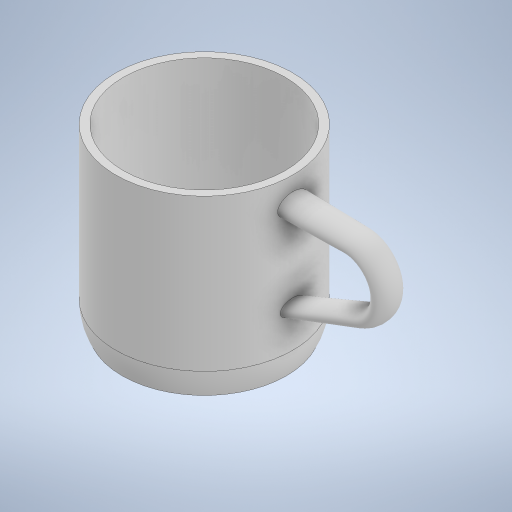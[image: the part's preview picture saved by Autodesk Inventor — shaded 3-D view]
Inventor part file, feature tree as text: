
AUTODESK INVENTOR PART (.ipt)
format: ipt  version: 2024 (Build 280153000, 153)  size: 358,912 bytes
history: native  units: mm
features: sketch x4, other x3, plane x2, revolve x1, shell x1, loft x1
ambient origin geometry x8: Origin, YZ Plane, XZ Plane, XY Plane, X Axis, Y Axis, Z Axis, Center Point
bodies: Body1 (feature_tree)
feature tree (12):
  other  "Sección transversal1"
  other  "Sólido1"
  revolve  "Revolución1"  [1 undecoded]
  shell  "Vaciado1"  Thickness=70.0mm
  sketch  "Boceto2"  dims[d3=32.5mm d4=90.0deg]
  other  "Punto de trabajo1"
  plane  "Plano de trabajo1"
  sketch  "Boceto3"  dims[d5=3.0mm]
  plane  "Plano de trabajo2"
  loft  "Solevación1"
  sketch  "Boceto1"  dims[d0=60.0mm d1=35.0mm d2=70.0mm]
  sketch  "Boceto4"  dims[d6=0.5mm d7=2.0mm d8=0.0mm d9=20.0mm d10=25.0mm d11=10.0mm d12=12.0mm d13=15.0mm d14=6.0mm d15=4.0mm d19=0.0mm d20=90.0deg d21=0.0mm d22=90.0deg d23=0.0mm d24=90.0deg]
note: 1 required parameter value undecoded (feature->parameter linkage not recoverable at this tier; creation-order binding heuristic only, values carry confidence <= 0.55)
